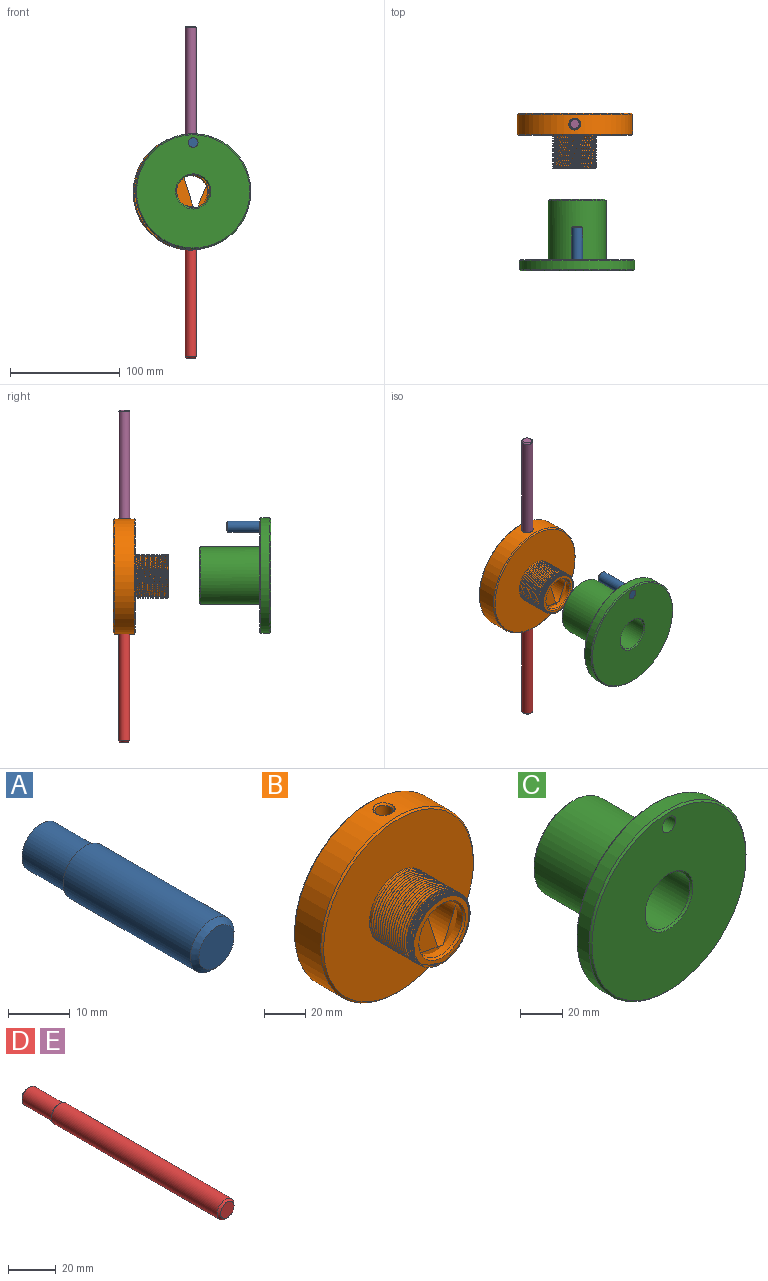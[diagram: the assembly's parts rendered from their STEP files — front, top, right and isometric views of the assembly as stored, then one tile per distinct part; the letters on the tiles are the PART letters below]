
ASSEMBLY  parts=5 mates=3
PART A: 6 faces, bbox 10x40x10 mm
  f0: cylinder r=4.4mm len=10mm, axis (0,1,0), area 276.5mm2, adj f1,f4
  f1: plane 8.8x8.8mm, normal (0,1,0), area 60.8mm2, adj f0
  f2: cylinder r=5mm len=29mm, axis (0,1,0), area 911.1mm2, adj f4,f5
  f3: plane 8x8mm, normal (0,-1,0), area 50.3mm2, adj f5
  f4: plane 10x10mm, normal (0,1,0), area 17.7mm2, adj f0,f2
  f5: cone r=4mm half-angle=45deg, axis (0,1,0), area 40mm2, adj f2,f3
PART B: 19 faces, bbox 106.2x52.1x106.2 mm
  f0: cylinder r=52.5mm len=105mm, axis (0,1,0), area 5772.9mm2, adj f8,f9,f14,f15
  f1: plane 103x103mm, normal (0,-1,0), area 7075.7mm2, adj f3,f9
  f2: plane 103x103mm, normal (0,1,0), area 7528mm2, adj f7,f8
  f3: cylinder r=20mm len=40mm, axis (0,1,0), area -640mm2, adj f1,f4,f16,f17,f18
  f4: plane 40.1x40.1mm, normal (0,-1,0), area 382.8mm2, adj f3,f6,f17,f18
  f5: cylinder r=15mm len=48mm, axis (0,1,0), area 4523.9mm2, adj f6,f7
  f6: cone r=16mm half-angle=45deg, axis (0,-1,0), area 137.7mm2, adj f4,f5
  f7: cone r=15mm half-angle=45deg, axis (0,1,0), area 137.7mm2, adj f2,f5
  f8: cone r=52.5mm half-angle=45deg, axis (0,-1,0), area 462.1mm2, adj f0,f2
  f9: cone r=51.5mm half-angle=45deg, axis (0,1,0), area 462.1mm2, adj f0,f1
  f10: cylinder r=4.4mm len=19.76mm, axis (0,0,1), area 542.6mm2, adj f11,f14
  f11: cone r=0mm half-angle=59deg, axis (0,0,1), area 71mm2, adj f10
  f12: cylinder r=4.4mm len=19.49mm, axis (0,0,-1), area 538.8mm2, adj f13,f15
  f13: cone r=0mm half-angle=59deg, axis (0,0,-1), area 71mm2, adj f12
  f14: bspline ~10.83x10.64mm, area 40.9mm2, adj f0,f10
  f15: bspline ~10.83x10.64mm, area 40.9mm2, adj f0,f12
  f16: plane 1.4x1.21mm, normal (0,0,-1), area 0.8mm2, adj f3,f17,f18
  f17: bspline ~46.19x40mm, area 3303.2mm2, adj f3,f4,f16,f18
  f18: bspline ~46.19x40mm, area 3352.3mm2, adj f3,f4,f16,f17
PART C: 15 faces, bbox 105x65x105 mm
  f0: cylinder r=15mm len=30.43mm, axis (0,-1,0), area 2868mm2, adj f10,f12
  f1: cylinder r=26.25mm len=54mm, axis (0,1,0), area 8906.4mm2, adj f5,f9
  f2: plane 50.5x50.5mm, normal (0,1,0), area 617.5mm2, adj f9,f11
  f3: cylinder r=52.5mm len=105mm, axis (0,1,0), area 2638.9mm2, adj f8,f13
  f4: plane 103x103mm, normal (0,-1,0), area 7467.2mm2, adj f8,f12,f14
  f5: plane 103x103mm, normal (0,1,0), area 6106.7mm2, adj f1,f13,f14
  f6: cylinder r=20mm len=40mm, axis (0,1,0), area 3644.2mm2, adj f7,f11
  f7: cone r=0mm half-angle=59deg, axis (0,1,0), area 587.2mm2, adj f6,f10
  f8: cone r=51.5mm half-angle=45deg, axis (0,1,0), area 462.1mm2, adj f3,f4
  f9: cone r=26.25mm half-angle=45deg, axis (0,-1,0), area 228.8mm2, adj f1,f2
  f10: cone r=15mm half-angle=29.5deg, axis (0,1,0), area 94.3mm2, adj f0,f7
  f11: cone r=20mm half-angle=45deg, axis (0,1,0), area 182.2mm2, adj f2,f6
  f12: cone r=15mm half-angle=45deg, axis (0,-1,0), area 137.7mm2, adj f0,f4
  f13: cone r=52.5mm half-angle=45deg, axis (0,-1,0), area 462.1mm2, adj f3,f5
  f14: cylinder r=4.4mm len=10mm, axis (0,-1,0), area 276.5mm2, adj f4,f5
PART D: 7 faces, bbox 10x118x10 mm
  f0: cylinder r=5mm len=98mm, axis (0,1,0), area 3078.8mm2, adj f4,f6
  f1: plane 8x8mm, normal (0,-1,0), area 50.3mm2, adj f6
  f2: cylinder r=4.4mm len=17.4mm, axis (0,-1,0), area 481mm2, adj f4,f5
  f3: plane 6.8x6.8mm, normal (0,1,0), area 36.3mm2, adj f5
  f4: cone r=5mm half-angle=45deg, axis (0,-1,0), area 25.1mm2, adj f0,f2
  f5: cone r=3.4mm half-angle=45deg, axis (0,-1,0), area 34.7mm2, adj f2,f3
  f6: cone r=4mm half-angle=45deg, axis (0,1,0), area 40mm2, adj f0,f1
PART E: same geometry as D
PLACE A rot(axis=(0,0,1),180deg) t=(25.54,3.24,55.32)mm
PLACE B t=(23.38,146.48,10.02)mm
PLACE C t=(25.54,68.24,10.82)mm
PLACE D rot(axis=(1,0,0),90deg) t=(23.38,136.48,-40.68)mm
PLACE E rot(axis=(-1,0,0),90deg) t=(23.38,136.48,61.32)mm
MATE fastened E.f0 <-> B.f10  axis (0,0,1) through (23.38,136.48,61.72)mm
MATE fastened D.f0 <-> B.f10  axis (0,0,-1) through (23.38,136.48,-41.68)mm
MATE fastened A.f0 <-> C.f14  axis (0,-1,0) through (25.54,13.24,55.32)mm
